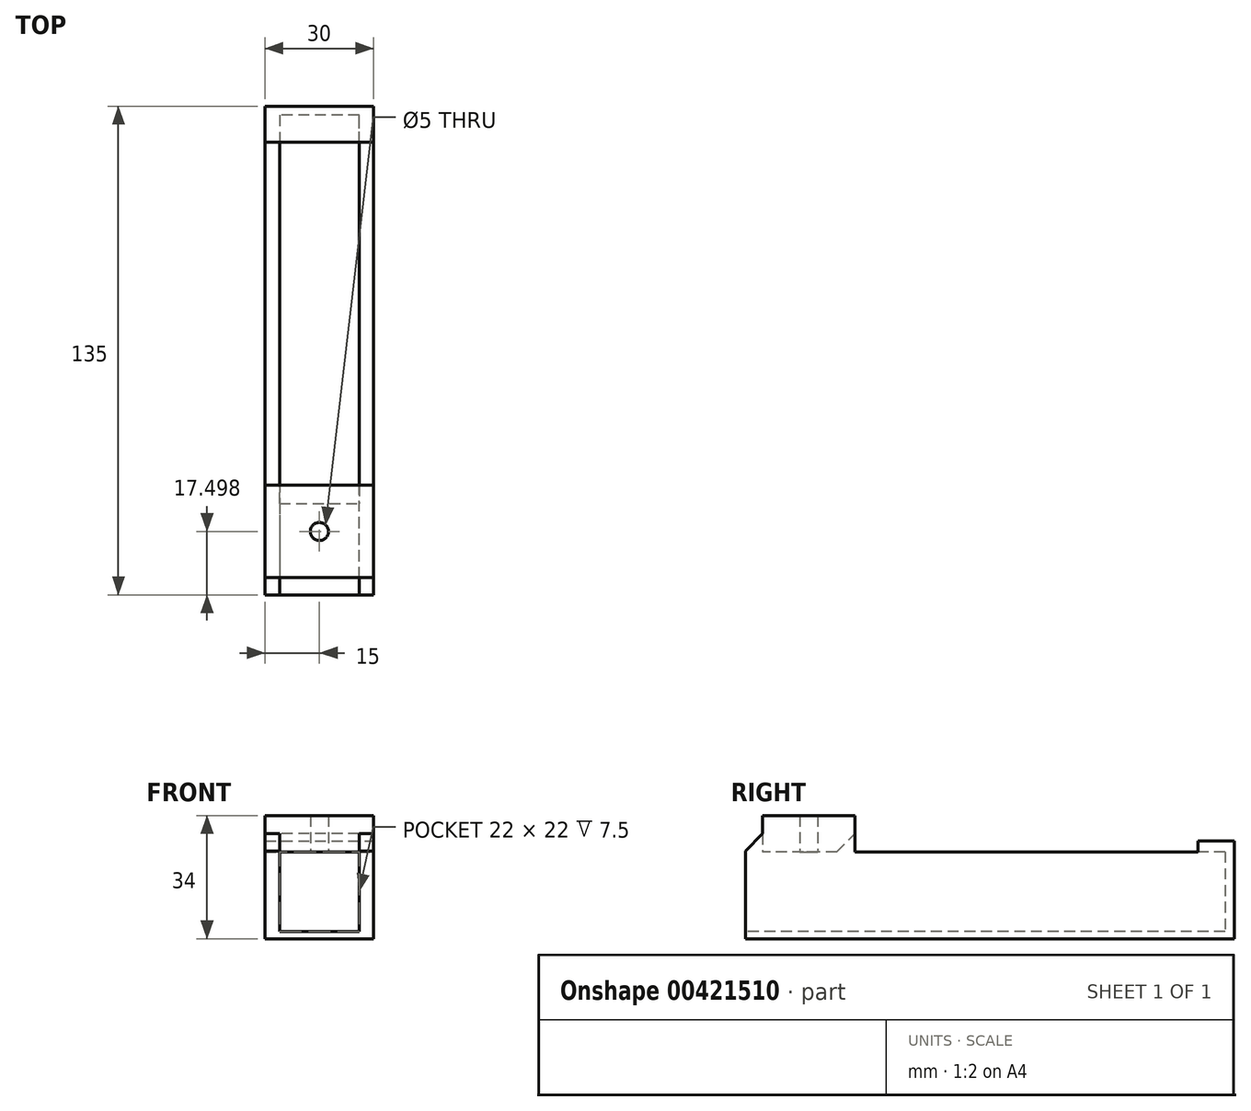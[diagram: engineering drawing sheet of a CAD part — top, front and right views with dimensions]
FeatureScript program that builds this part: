
annotation { "Feature Type Name" : "Feature", "Feature Type Description" : "" }
export const myFeature = defineFeature(function(context is Context, id is Id, definition is map)
    precondition{}
    {
        {
            var Q0;
            Q0=qCreatedBy(makeId("Top.planeOp"),FACE);
            var sketch = newSketch(context, id + "F0", { "sketchPlane" : qUnion([Q0])});
            skLineSegment(sketch, "E0.bottom", {"start": v(130.73, 27.14) * mm, "end": v(160.73, 27.14) * mm});
            skLineSegment(sketch, "E0.top", {"start": v(130.73, -107.86) * mm, "end": v(134.73, -107.86) * mm});
            skLineSegment(sketch, "E0.left", {"start": v(130.73, 27.14) * mm, "end": v(130.73, -107.86) * mm});
            skLineSegment(sketch, "E0.right", {"start": v(160.73, 27.14) * mm, "end": v(160.73, -107.86) * mm});
            skLineSegment(sketch, "E1.top", {"start": v(156.73, 24.64) * mm, "end": v(134.73, 24.64) * mm});
            skLineSegment(sketch, "E1.left", {"start": v(156.73, -105.36) * mm, "end": v(156.73, 24.64) * mm});
            skLineSegment(sketch, "E1.right", {"start": v(134.73, -105.36) * mm, "end": v(134.73, 24.64) * mm});
            skPoint(sketch, "E1.middle", {"position": v(145.73, -40.36) * mm});
            skPoint(sketch, "E1.middle.positionSnap0", {"position": v(145.73, 27.14) * mm});
            skPoint(sketch, "E1.middle.positionSnap1", {"position": v(130.73, -40.36) * mm});
            skPoint(sketch, "E1.centerSnap0", {"position": v(145.73, 27.14) * mm});
            skPoint(sketch, "E1.centerSnap1", {"position": v(130.73, -40.36) * mm});
            skLineSegment(sketch, "E2", {"start": v(134.73, -105.36) * mm, "end": v(134.73, -107.86) * mm});
            skLineSegment(sketch, "E3", {"start": v(156.73, -105.36) * mm, "end": v(156.73, -107.86) * mm});
            skLineSegment(sketch, "E4.trimOffspring", {"start": v(156.73, -107.86) * mm, "end": v(160.73, -107.86) * mm});
            skLineSegment(sketch, "E5", {"start": v(145.73, 24.64) * mm, "end": v(145.73, 27.14) * mm, "construction": true});
            skSolve(sketch);
        }
        {
            var Q0;
            Q0 = qSketchRegion(id + "F0", true);
            extrude(context, id + "F1", {"entities" : qUnion([Q0]), "depth" : 22 * mm});
        }
        {
            var Q0;
            Q0=makeQuery(id+"F1.opExtrude","CAP_FACE",FACE,{"disambiguationData":[OSD([sQuery(id+"F0.wireOp",EDGE,"E0.bottom"),sQuery(id+"F0.wireOp",EDGE,"E0.top"),sQuery(id+"F0.wireOp",EDGE,"E0.left"),sQuery(id+"F0.wireOp",EDGE,"E0.right"),sQuery(id+"F0.wireOp",EDGE,"E1.top"),sQuery(id+"F0.wireOp",EDGE,"E1.left"),sQuery(id+"F0.wireOp",EDGE,"E1.right"),sQuery(id+"F0.wireOp",EDGE,"E2"),sQuery(id+"F0.wireOp",EDGE,"E3"),sQuery(id+"F0.wireOp",EDGE,"E4.trimOffspring")])],"isStart":true});
            var sketch = newSketch(context, id + "F2", { "sketchPlane" : qUnion([Q0])});
            skLineSegment(sketch, "E6.bottom", {"start": v(130.73, 107.86) * mm, "end": v(160.73, 107.86) * mm});
            skLineSegment(sketch, "E6.top", {"start": v(130.73, -27.14) * mm, "end": v(160.73, -27.14) * mm});
            skLineSegment(sketch, "E6.left", {"start": v(130.73, 107.86) * mm, "end": v(130.73, -27.14) * mm});
            skLineSegment(sketch, "E6.right", {"start": v(160.73, 107.86) * mm, "end": v(160.73, -27.14) * mm});
            skSolve(sketch);
        }
        {
            var Q0;
            Q0 = qSketchRegion(id + "F2", true);
            extrude(context, id + "F3", {"entities" : qUnion([Q0]), "operationType" : NewBodyOperationType.ADD, "depth" : 2 * mm});
        }
        {
            var Q0;
            Q0=makeQuery(id+"F1.opExtrude","CAP_FACE",FACE,{"disambiguationData":[OSD([sQuery(id+"F0.wireOp",EDGE,"E0.bottom"),sQuery(id+"F0.wireOp",EDGE,"E0.top"),sQuery(id+"F0.wireOp",EDGE,"E0.left"),sQuery(id+"F0.wireOp",EDGE,"E0.right"),sQuery(id+"F0.wireOp",EDGE,"E1.top"),sQuery(id+"F0.wireOp",EDGE,"E1.left"),sQuery(id+"F0.wireOp",EDGE,"E1.right"),sQuery(id+"F0.wireOp",EDGE,"E2"),sQuery(id+"F0.wireOp",EDGE,"E3"),sQuery(id+"F0.wireOp",EDGE,"E4.trimOffspring")])],"isStart":false});
            var sketch = newSketch(context, id + "F4", { "sketchPlane" : qUnion([Q0])});
            skLineSegment(sketch, "E7.bottom", {"start": v(130.73, 27.14) * mm, "end": v(160.73, 27.14) * mm, "construction": true});
            skLineSegment(sketch, "E7.top", {"start": v(130.73, -107.86) * mm, "end": v(160.73, -107.86) * mm, "construction": true});
            skLineSegment(sketch, "E7.left", {"start": v(130.73, 27.14) * mm, "end": v(130.73, -107.86) * mm, "construction": true});
            skLineSegment(sketch, "E7.right", {"start": v(160.73, 27.14) * mm, "end": v(160.73, -107.86) * mm, "construction": true});
            skLineSegment(sketch, "E8.bottom", {"start": v(134.73, 24.64) * mm, "end": v(156.73, 24.64) * mm, "construction": true});
            skLineSegment(sketch, "E8.top", {"start": v(134.73, -90.36) * mm, "end": v(156.73, -90.36) * mm, "construction": true});
            skLineSegment(sketch, "E8.left", {"start": v(134.73, 24.64) * mm, "end": v(134.73, -90.36) * mm, "construction": true});
            skLineSegment(sketch, "E8.right", {"start": v(156.73, 24.64) * mm, "end": v(156.73, -90.36) * mm, "construction": true});
            skLineSegment(sketch, "E9.bottom", {"start": v(160.73, -77.6) * mm, "end": v(130.73, -77.6) * mm});
            skLineSegment(sketch, "E9.top", {"start": v(160.73, -103.11) * mm, "end": v(130.73, -103.11) * mm});
            skLineSegment(sketch, "E9.left", {"start": v(160.73, -77.6) * mm, "end": v(160.73, -103.11) * mm});
            skLineSegment(sketch, "E9.right", {"start": v(130.73, -77.6) * mm, "end": v(130.73, -103.11) * mm});
            skPoint(sketch, "E9.middle", {"position": v(145.73, -90.36) * mm});
            skCircle(sketch, "E10", {"center": v(145.73, -90.36) * mm, "radius": 2.5 * mm});
            skSolve(sketch);
        }
        {
            var Q0;
            Q0 = qSketchRegion(id + "F4", true);
            extrude(context, id + "F5", {"entities" : qUnion([Q0]), "operationType" : NewBodyOperationType.ADD, "depth" : 10 * mm});
        }
        {
            var Q0;
            {var subQ0=sQuery(id+"F0.wireOp",EDGE,"E2");var subQ1=sQuery(id+"F0.wireOp",EDGE,"E1.right");var subQ2=sQuery(id+"F0.wireOp",EDGE,"E3");var subQ3=sQuery(id+"F0.wireOp",EDGE,"E1.left");var subQ4=sQuery(id+"F0.wireOp",EDGE,"E0.bottom");var subQ5=sQuery(id+"F0.wireOp",EDGE,"E0.right");var subQ6=sQuery(id+"F0.wireOp",EDGE,"E0.left");var subQ7=sQuery(id+"F4.wireOp",EDGE,"E9.bottom");var subQ8=sQuery(id+"F0.wireOp",EDGE,"E1.top");var subQ9=sQuery(id+"F4.wireOp",EDGE,"E9.right");var subQ10=sQuery(id+"F4.wireOp",EDGE,"E9.left");Q0=makeQuery(id+"F5.boolean.opBoolean","SPLIT",FACE,{"disambiguationData":[TD([makeQuery(id+"F1.opExtrude","SWEPT_FACE",FACE,{"disambiguationData":[OSD([subQ4])]}),makeQuery(id+"F1.opExtrude","SWEPT_FACE",FACE,{"disambiguationData":[OSD([subQ6])]}),makeQuery(id+"F1.opExtrude","SWEPT_FACE",FACE,{"disambiguationData":[OSD([subQ5])]}),makeQuery(id+"F1.opExtrude","SWEPT_FACE",FACE,{"disambiguationData":[OSD([subQ8])]}),makeQuery(id+"F1.opExtrude","SWEPT_FACE",FACE,{"disambiguationData":[OSD([subQ3,subQ2])]}),makeQuery(id+"F1.opExtrude","SWEPT_FACE",FACE,{"disambiguationData":[OSD([subQ1,subQ0])]}),makeQuery(id+"F3.opExtrude","SWEPT_FACE",FACE,{"disambiguationData":[OSD([sQuery(id+"F2.wireOp",EDGE,"E6.top")])]}),makeQuery(id+"F3.opExtrude","SWEPT_FACE",FACE,{"disambiguationData":[OSD([sQuery(id+"F2.wireOp",EDGE,"E6.left")])]}),makeQuery(id+"F3.opExtrude","SWEPT_FACE",FACE,{"disambiguationData":[OSD([sQuery(id+"F2.wireOp",EDGE,"E6.right")])]}),makeQuery(id+"F5.opExtrude","SWEPT_FACE",FACE,{"disambiguationData":[OSD([subQ7])]}),makeQuery(id+"F5.opExtrude","CAP_FACE",FACE,{"disambiguationData":[OSD([subQ7,sQuery(id+"F4.wireOp",EDGE,"E9.top"),subQ10,subQ9,sQuery(id+"F4.wireOp",EDGE,"E10")])],"isStart":true}),makeQuery(id+"F5.opExtrude","SWEPT_FACE",FACE,{"disambiguationData":[OSD([subQ10])]}),makeQuery(id+"F5.opExtrude","SWEPT_FACE",FACE,{"disambiguationData":[OSD([subQ9])]})])],"derivedFrom":makeQuery(id+"F1.opExtrude","CAP_FACE",FACE,{"disambiguationData":[OSD([subQ4,sQuery(id+"F0.wireOp",EDGE,"E0.top"),subQ6,subQ5,subQ8,subQ3,subQ1,subQ0,subQ2,sQuery(id+"F0.wireOp",EDGE,"E4.trimOffspring")])],"isStart":false})});}
            var sketch = newSketch(context, id + "F6", { "sketchPlane" : qUnion([Q0])});
            skLineSegment(sketch, "E11.bottom", {"start": v(130.73, 27.14) * mm, "end": v(160.73, 27.14) * mm});
            skLineSegment(sketch, "E11.top", {"start": v(130.73, 17.14) * mm, "end": v(160.73, 17.14) * mm});
            skLineSegment(sketch, "E11.left", {"start": v(130.73, 27.14) * mm, "end": v(130.73, 17.14) * mm});
            skLineSegment(sketch, "E11.right", {"start": v(160.73, 27.14) * mm, "end": v(160.73, 17.14) * mm});
            skSolve(sketch);
        }
        {
            var Q0;
            Q0 = qSketchRegion(id + "F6", true);
            extrude(context, id + "F7", {"entities" : qUnion([Q0]), "operationType" : NewBodyOperationType.ADD, "depth" : 3 * mm});
        }
        {
            var Q0;
            {var subQ0=sQuery(id+"F0.wireOp",EDGE,"E2");var subQ1=sQuery(id+"F0.wireOp",EDGE,"E1.right");var subQ2=sQuery(id+"F0.wireOp",EDGE,"E0.left");var subQ3=makeQuery(id+"F1.opExtrude","CAP_FACE",FACE,{"disambiguationData":[OSD([sQuery(id+"F0.wireOp",EDGE,"E0.bottom"),sQuery(id+"F0.wireOp",EDGE,"E0.top"),subQ2,sQuery(id+"F0.wireOp",EDGE,"E0.right"),sQuery(id+"F0.wireOp",EDGE,"E1.top"),sQuery(id+"F0.wireOp",EDGE,"E1.left"),subQ1,subQ0,sQuery(id+"F0.wireOp",EDGE,"E3"),sQuery(id+"F0.wireOp",EDGE,"E4.trimOffspring")])],"isStart":false});var subQ5=sQuery(id+"F4.wireOp",EDGE,"E9.top");var subQ6=makeQuery(id+"F5.opExtrude","SWEPT_FACE",FACE,{"disambiguationData":[OSD([subQ5])]});Q0=makeQuery(id+"F5.boolean.opBoolean","SPLIT",EDGE,{"disambiguationData":[topologyDisambiguationEdgeConnected([subQ3,subQ6]),TD([makeQuery(id+"F1.opExtrude","SWEPT_FACE",FACE,{"disambiguationData":[OSD([subQ2])]})])],"derivedFrom":makeQuery(id+"F5.opExtrude","CAP_EDGE",EDGE,{"disambiguationData":[OSD([subQ5])],"isStart":true})});}
            var Q1;
            {var subQ0=sQuery(id+"F0.wireOp",EDGE,"E0.right");var subQ1=sQuery(id+"F0.wireOp",EDGE,"E3");var subQ2=sQuery(id+"F0.wireOp",EDGE,"E1.left");var subQ4=sQuery(id+"F4.wireOp",EDGE,"E9.top");var subQ5=makeQuery(id+"F1.opExtrude","CAP_FACE",FACE,{"disambiguationData":[OSD([sQuery(id+"F0.wireOp",EDGE,"E0.bottom"),sQuery(id+"F0.wireOp",EDGE,"E0.top"),sQuery(id+"F0.wireOp",EDGE,"E0.left"),subQ0,sQuery(id+"F0.wireOp",EDGE,"E1.top"),subQ2,sQuery(id+"F0.wireOp",EDGE,"E1.right"),sQuery(id+"F0.wireOp",EDGE,"E2"),subQ1,sQuery(id+"F0.wireOp",EDGE,"E4.trimOffspring")])],"isStart":false});var subQ6=makeQuery(id+"F5.opExtrude","SWEPT_FACE",FACE,{"disambiguationData":[OSD([subQ4])]});Q1=makeQuery(id+"F5.boolean.opBoolean","SPLIT",EDGE,{"disambiguationData":[topologyDisambiguationEdgeConnected([subQ5,subQ6]),TD([makeQuery(id+"F1.opExtrude","SWEPT_FACE",FACE,{"disambiguationData":[OSD([subQ0])]})])],"derivedFrom":makeQuery(id+"F5.opExtrude","CAP_EDGE",EDGE,{"disambiguationData":[OSD([subQ4])],"isStart":true})});}
            var Q2;
            {var subQ0=sQuery(id+"F4.wireOp",EDGE,"E9.bottom");var subQ1=makeQuery(id+"F5.opExtrude","SWEPT_FACE",FACE,{"disambiguationData":[OSD([subQ0])]});var subQ2=sQuery(id+"F0.wireOp",EDGE,"E0.right");var subQ3=sQuery(id+"F0.wireOp",EDGE,"E3");var subQ4=sQuery(id+"F0.wireOp",EDGE,"E1.left");var subQ6=makeQuery(id+"F1.opExtrude","CAP_FACE",FACE,{"disambiguationData":[OSD([sQuery(id+"F0.wireOp",EDGE,"E0.bottom"),sQuery(id+"F0.wireOp",EDGE,"E0.top"),sQuery(id+"F0.wireOp",EDGE,"E0.left"),subQ2,sQuery(id+"F0.wireOp",EDGE,"E1.top"),subQ4,sQuery(id+"F0.wireOp",EDGE,"E1.right"),sQuery(id+"F0.wireOp",EDGE,"E2"),subQ3,sQuery(id+"F0.wireOp",EDGE,"E4.trimOffspring")])],"isStart":false});Q2=makeQuery(id+"F5.boolean.opBoolean","SPLIT",EDGE,{"disambiguationData":[topologyDisambiguationEdgeConnected([subQ6,subQ1]),TD([makeQuery(id+"F1.opExtrude","SWEPT_FACE",FACE,{"disambiguationData":[OSD([subQ2])]})])],"derivedFrom":makeQuery(id+"F5.opExtrude","CAP_EDGE",EDGE,{"disambiguationData":[OSD([subQ0])],"isStart":true})});}
            var Q3;
            {var subQ0=sQuery(id+"F0.wireOp",EDGE,"E2");var subQ1=sQuery(id+"F0.wireOp",EDGE,"E1.right");var subQ2=sQuery(id+"F0.wireOp",EDGE,"E0.left");var subQ3=makeQuery(id+"F1.opExtrude","CAP_FACE",FACE,{"disambiguationData":[OSD([sQuery(id+"F0.wireOp",EDGE,"E0.bottom"),sQuery(id+"F0.wireOp",EDGE,"E0.top"),subQ2,sQuery(id+"F0.wireOp",EDGE,"E0.right"),sQuery(id+"F0.wireOp",EDGE,"E1.top"),sQuery(id+"F0.wireOp",EDGE,"E1.left"),subQ1,subQ0,sQuery(id+"F0.wireOp",EDGE,"E3"),sQuery(id+"F0.wireOp",EDGE,"E4.trimOffspring")])],"isStart":false});var subQ4=sQuery(id+"F4.wireOp",EDGE,"E9.bottom");var subQ5=makeQuery(id+"F5.opExtrude","SWEPT_FACE",FACE,{"disambiguationData":[OSD([subQ4])]});Q3=makeQuery(id+"F5.boolean.opBoolean","SPLIT",EDGE,{"disambiguationData":[topologyDisambiguationEdgeConnected([subQ3,subQ5]),TD([makeQuery(id+"F1.opExtrude","SWEPT_FACE",FACE,{"disambiguationData":[OSD([subQ2])]})])],"derivedFrom":makeQuery(id+"F5.opExtrude","CAP_EDGE",EDGE,{"disambiguationData":[OSD([subQ4])],"isStart":true})});}
            chamfer(context, id + "F8", {"entities" : qUnion([Q0, Q1, Q2, Q3]), "width" : 5 * mm, "tangentPropagation" : true});
        }
    });
